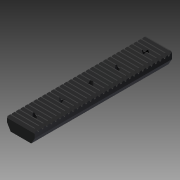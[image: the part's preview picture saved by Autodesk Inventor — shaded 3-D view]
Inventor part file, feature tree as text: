
AUTODESK INVENTOR PART (.ipt)
format: ipt  version: 2014 SP2 (Build 180246200, 246)  size: 509,440 bytes
history: native  units: in
note: dims shown in document units (in); Inventor stores cm internally (conversion verified against a paired STEP export)
features: other x5, extrude x1, imported_body x1, sketch x1
ambient origin geometry x8: Origin, YZ Plane, XZ Plane, XY Plane, X Axis, Y Axis, Z Axis, Center Point
bodies: Body1 (feature_tree)
feature tree (8):
  other  "Rack"
  other  "Rack1"
  other  "FRONT"
  other  "TOP"
  other  "RIGHT"
  extrude  "Extrusion1"  [1 undecoded]
  imported_body  "Base1"
  sketch  "Sketch1"  dims[d0=3.937in d1=0.0in]
note: 1 required parameter value undecoded (feature->parameter linkage not recoverable at this tier; creation-order binding heuristic only, values carry confidence <= 0.55)
